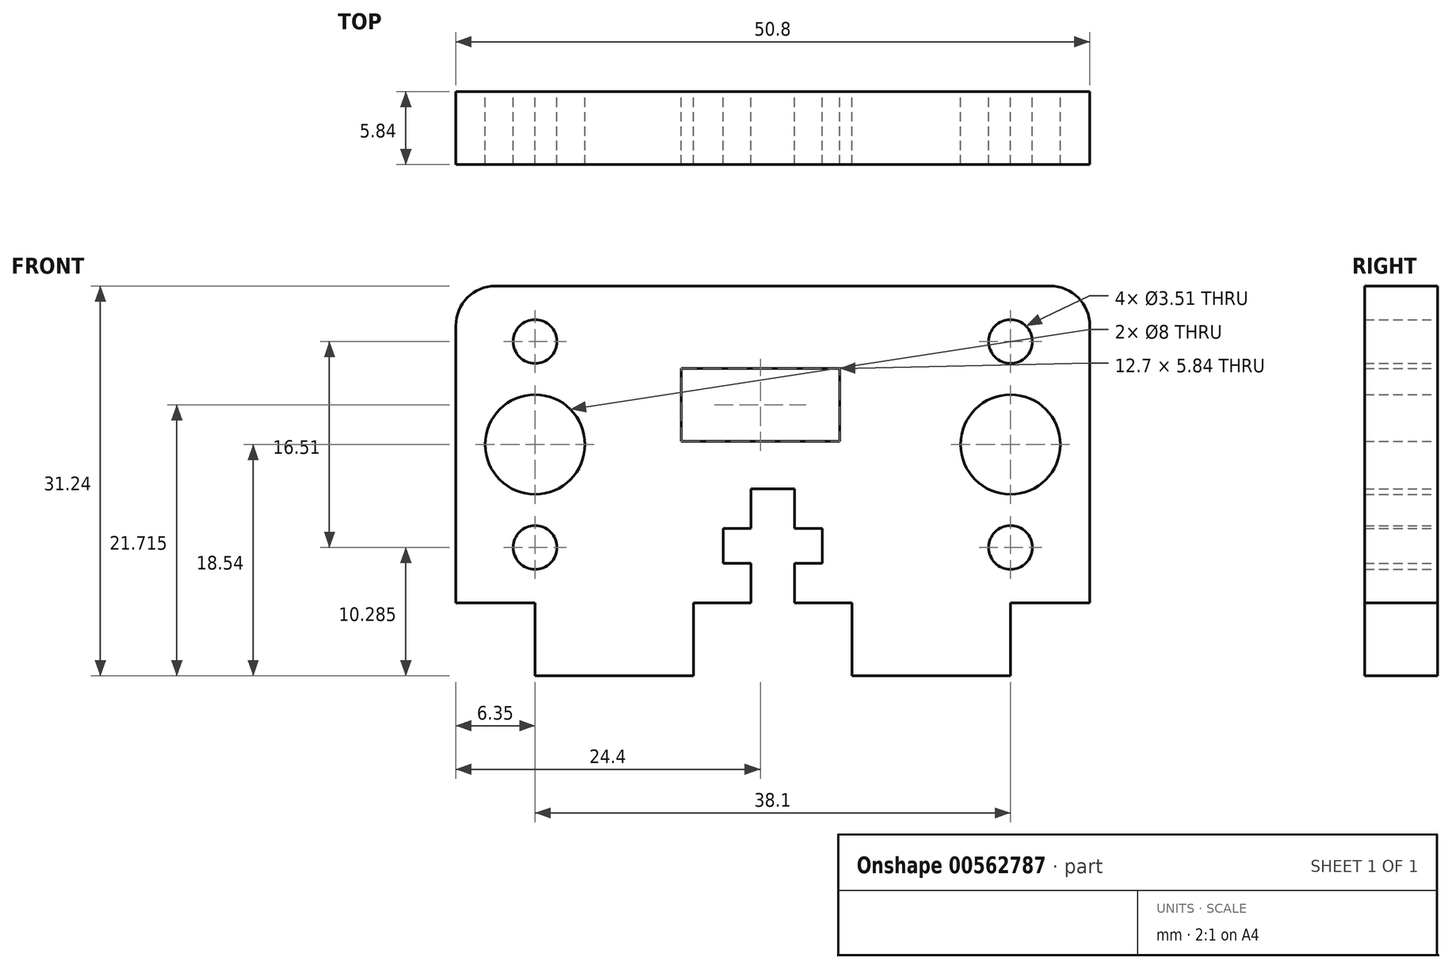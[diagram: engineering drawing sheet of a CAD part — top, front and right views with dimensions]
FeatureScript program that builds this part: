
annotation { "Feature Type Name" : "Feature", "Feature Type Description" : "" }
export const myFeature = defineFeature(function(context is Context, id is Id, definition is map)
    precondition{}
    {
        {
            var Q0;
            Q0=qCreatedBy(makeId("Front.planeOp"),FACE);
            var sketch = newSketch(context, id + "F0", { "sketchPlane" : qUnion([Q0])});
            skLineSegment(sketch, "E0.bottom", {"start": v(-25.4, 12.7) * mm, "end": v(-12.7, 12.7) * mm});
            skLineSegment(sketch, "E0.top", {"start": v(-25.4, -12.7) * mm, "end": v(-19.05, -12.7) * mm});
            skLineSegment(sketch, "E0.left", {"start": v(-25.4, 12.7) * mm, "end": v(-25.4, -12.7) * mm});
            skLineSegment(sketch, "E0.right", {"start": v(25.4, 12.7) * mm, "end": v(25.4, -12.7) * mm});
            skPoint(sketch, "E0.middle", {"position": v(0, 0) * mm});
            skLineSegment(sketch, "E1.top", {"start": v(-19.05, -18.54) * mm, "end": v(-6.35, -18.54) * mm});
            skLineSegment(sketch, "E1.left", {"start": v(-19.05, -12.7) * mm, "end": v(-19.05, -18.54) * mm});
            skLineSegment(sketch, "E1.right", {"start": v(-6.35, -12.7) * mm, "end": v(-6.35, -18.54) * mm});
            skPoint(sketch, "E1.middle", {"position": v(-12.7, -15.62) * mm});
            skLineSegment(sketch, "E2.MirrorCS", {"start": v(6.35, -12.7) * mm, "end": v(6.35, -18.54) * mm});
            skLineSegment(sketch, "E3.MirrorCS", {"start": v(19.05, -12.7) * mm, "end": v(19.05, -18.54) * mm});
            skLineSegment(sketch, "E4.MirrorCS", {"start": v(25.4, -12.7) * mm, "end": v(19.05, -12.7) * mm});
            skLineSegment(sketch, "E5.MirrorCS", {"start": v(19.05, -18.54) * mm, "end": v(6.35, -18.54) * mm});
            skPoint(sketch, "E6.MirrorP", {"position": v(12.7, -15.62) * mm});
            skLineSegment(sketch, "E7.trimOffspring", {"start": v(-19.05, -12.7) * mm, "end": v(-25.4, -12.7) * mm});
            skLineSegment(sketch, "E8.trimOffspring", {"start": v(6.35, -12.7) * mm, "end": v(1.75, -12.7) * mm});
            skLineSegment(sketch, "E9.trimOffspring", {"start": v(19.05, -12.7) * mm, "end": v(25.4, -12.7) * mm});
            skLineSegment(sketch, "E10.trimOffspring", {"start": v(-6.35, -12.7) * mm, "end": v(-1.75, -12.7) * mm});
            skCircle(sketch, "E11", {"center": v(-19.05, 0) * mm, "radius": 4 * mm});
            skLineSegment(sketch, "E12", {"start": v(-19.05, 12.7) * mm, "end": v(-19.05, -12.7) * mm, "construction": true});
            skCircle(sketch, "E13", {"center": v(-19.05, 8.26) * mm, "radius": 1.75 * mm});
            skCircle(sketch, "E14.MirrorC", {"center": v(-19.05, -8.26) * mm, "radius": 1.75 * mm});
            skLineSegment(sketch, "E15.MirrorCS", {"start": v(19.05, 12.7) * mm, "end": v(19.05, -12.7) * mm, "construction": true});
            skCircle(sketch, "E16.MirrorC", {"center": v(19.05, -8.26) * mm, "radius": 1.75 * mm});
            skCircle(sketch, "E17.MirrorC", {"center": v(19.05, 8.26) * mm, "radius": 1.75 * mm});
            skCircle(sketch, "E18.MirrorC", {"center": v(19.05, 0) * mm, "radius": 4 * mm});
            skLineSegment(sketch, "E19.left", {"start": v(-1.75, -12.7) * mm, "end": v(-1.75, -9.52) * mm});
            skLineSegment(sketch, "E19.right", {"start": v(1.75, -12.7) * mm, "end": v(1.75, -9.52) * mm});
            skPoint(sketch, "E19.middle", {"position": v(0, -11.11) * mm});
            skLineSegment(sketch, "E20.bottom", {"start": v(-3.97, -9.52) * mm, "end": v(-1.75, -9.52) * mm});
            skLineSegment(sketch, "E20.top", {"start": v(-3.97, -6.75) * mm, "end": v(-1.75, -6.75) * mm});
            skLineSegment(sketch, "E20.left", {"start": v(-3.97, -9.52) * mm, "end": v(-3.97, -6.75) * mm});
            skLineSegment(sketch, "E20.right", {"start": v(3.97, -9.52) * mm, "end": v(3.97, -6.75) * mm});
            skPoint(sketch, "E20.middle", {"position": v(0, -8.14) * mm});
            skLineSegment(sketch, "E21.top", {"start": v(-1.75, -3.57) * mm, "end": v(1.75, -3.57) * mm});
            skLineSegment(sketch, "E21.left", {"start": v(-1.75, -6.75) * mm, "end": v(-1.75, -3.57) * mm});
            skLineSegment(sketch, "E21.right", {"start": v(1.75, -6.75) * mm, "end": v(1.75, -3.57) * mm});
            skPoint(sketch, "E21.middle", {"position": v(0, -5.16) * mm});
            skLineSegment(sketch, "E22.trimOffspring", {"start": v(1.75, -6.75) * mm, "end": v(3.97, -6.75) * mm});
            skLineSegment(sketch, "E23.trimOffspring", {"start": v(1.75, -9.52) * mm, "end": v(3.97, -9.52) * mm});
            skLineSegment(sketch, "E24.trimOffspring", {"start": v(-1.75, -12.7) * mm, "end": v(-6.35, -12.7) * mm});
            skLineSegment(sketch, "E25.trimOffspring", {"start": v(1.75, -12.7) * mm, "end": v(6.35, -12.7) * mm});
            skLineSegment(sketch, "E26.trimOffspring", {"start": v(12.7, 12.7) * mm, "end": v(25.4, 12.7) * mm});
            skPoint(sketch, "E27.orphan", {"position": v(-6.35, 0) * mm});
            skPoint(sketch, "E28.orphan", {"position": v(6.35, 0) * mm});
            skPoint(sketch, "E29.start.orphan", {"position": v(-9.52, 6.35) * mm});
            skPoint(sketch, "E30.MirrorCS.end.orphan", {"position": v(9.52, 6.35) * mm});
            skLineSegment(sketch, "E31", {"start": v(-12.7, 12.7) * mm, "end": v(12.7, 12.7) * mm});
            skLineSegment(sketch, "E32.bottom", {"start": v(-7.35, 0.25) * mm, "end": v(5.35, 0.25) * mm});
            skLineSegment(sketch, "E32.top", {"start": v(-7.35, 6.1) * mm, "end": v(5.35, 6.1) * mm});
            skLineSegment(sketch, "E32.left", {"start": v(-7.35, 0.25) * mm, "end": v(-7.35, 6.1) * mm});
            skLineSegment(sketch, "E32.right", {"start": v(5.35, 0.25) * mm, "end": v(5.35, 6.1) * mm});
            skPoint(sketch, "E32.middle", {"position": v(-1.7, 3.17) * mm});
            skSolve(sketch);
        }
        {
            var Q0;
            Q0 = qSketchRegion(id + "F0", true);
            extrude(context, id + "F1", {"entities" : qUnion([Q0]), "depth" : 5.84 * mm, "offsetDistance" : 25.4 * mm});
        }
        {
            var Q0;
            Q0=makeQuery(id+"F1.opExtrude","SWEPT_EDGE",EDGE,{"disambiguationData":[OSD([sQuery(id+"F0.wireOp",EDGE,"4JrDi54b-J1pj-Y84I-09Nl-TX9jd4DHeLI8"),sQuery(id+"F0.wireOp",EDGE,"E29")])]});
            var Q1;
            Q1=makeQuery(id+"F1.opExtrude","SWEPT_EDGE",EDGE,{"disambiguationData":[OSD([sQuery(id+"F0.wireOp",EDGE,"E0.bottom"),sQuery(id+"F0.wireOp",EDGE,"4JrDi54b-J1pj-Y84I-09Nl-TX9jd4DHeLI8")])]});
            var Q2;
            Q2=makeQuery(id+"F1.opExtrude","SWEPT_EDGE",EDGE,{"disambiguationData":[OSD([sQuery(id+"F0.wireOp",EDGE,"E0.bottom"),sQuery(id+"F0.wireOp",EDGE,"E0.left")])]});
            var Q3;
            Q3=makeQuery(id+"F1.opExtrude","SWEPT_EDGE",EDGE,{"disambiguationData":[OSD([sQuery(id+"F0.wireOp",EDGE,"E30.MirrorCS"),sQuery(id+"F0.wireOp",EDGE,"E29")])]});
            var Q4;
            Q4=makeQuery(id+"F1.opExtrude","SWEPT_EDGE",EDGE,{"disambiguationData":[OSD([sQuery(id+"F0.wireOp",EDGE,"E30.MirrorCS"),sQuery(id+"F0.wireOp",EDGE,"E26.trimOffspring")])]});
            var Q5;
            Q5=makeQuery(id+"F1.opExtrude","SWEPT_EDGE",EDGE,{"disambiguationData":[OSD([sQuery(id+"F0.wireOp",EDGE,"E0.right"),sQuery(id+"F0.wireOp",EDGE,"E26.trimOffspring")])]});
            fillet(context, id + "F2", {"entities" : qUnion([Q0, Q1, Q2, Q3, Q4, Q5]), "radius" : 3.17 * mm, "tangentPropagation" : true, "allowEdgeOverflow" : false});
        }
    });
